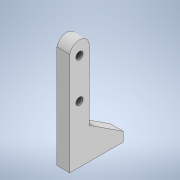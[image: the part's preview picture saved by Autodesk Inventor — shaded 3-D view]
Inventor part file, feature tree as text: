
AUTODESK INVENTOR PART (.ipt)
format: ipt  version: 2020 (Build 240168000, 168)  size: 136,192 bytes
history: native  units: in
note: dims shown in document units (in); Inventor stores cm internally (conversion verified against a paired STEP export)
features: extrude x6, sketch x6
ambient origin geometry x8: Origin, YZ Plane, XZ Plane, XY Plane, X Axis, Y Axis, Z Axis, Center Point
bodies: Solid1 (feature_tree)
feature tree (12):
  extrude  "Extrusion1"  Depth=0.375in
  extrude  "Extrusion2"  Depth=0.25in
  extrude  "Extrusion3"  Depth=0.141in
  extrude  "Extrusion4"  Depth=0.25in TaperAngle=0.0deg
  extrude  "Extrusion5"  Depth=1.0in
  extrude  "Extrusion6"  Depth=0.25in TaperAngle=0.0deg
  sketch  "Sketch1"  dims[d0=1.0in d1=0.375in]
  sketch  "Sketch2"  dims[d2=0.25in d3=0.0in d4=0.77in]
  sketch  "Sketch3"  dims[d5=0.141in d6=0.141in]
  sketch  "Sketch4"  dims[d7=0.5625in d8=0.0in d9=0.25in d10=0.0in]
  sketch  "Sketch5"  dims[d13=0.25in d14=0.0in d15=1.0in]
  sketch  "Sketch6"  dims[d16=0.25in d17=0.0in d18=2.5in d19=0.0in]
